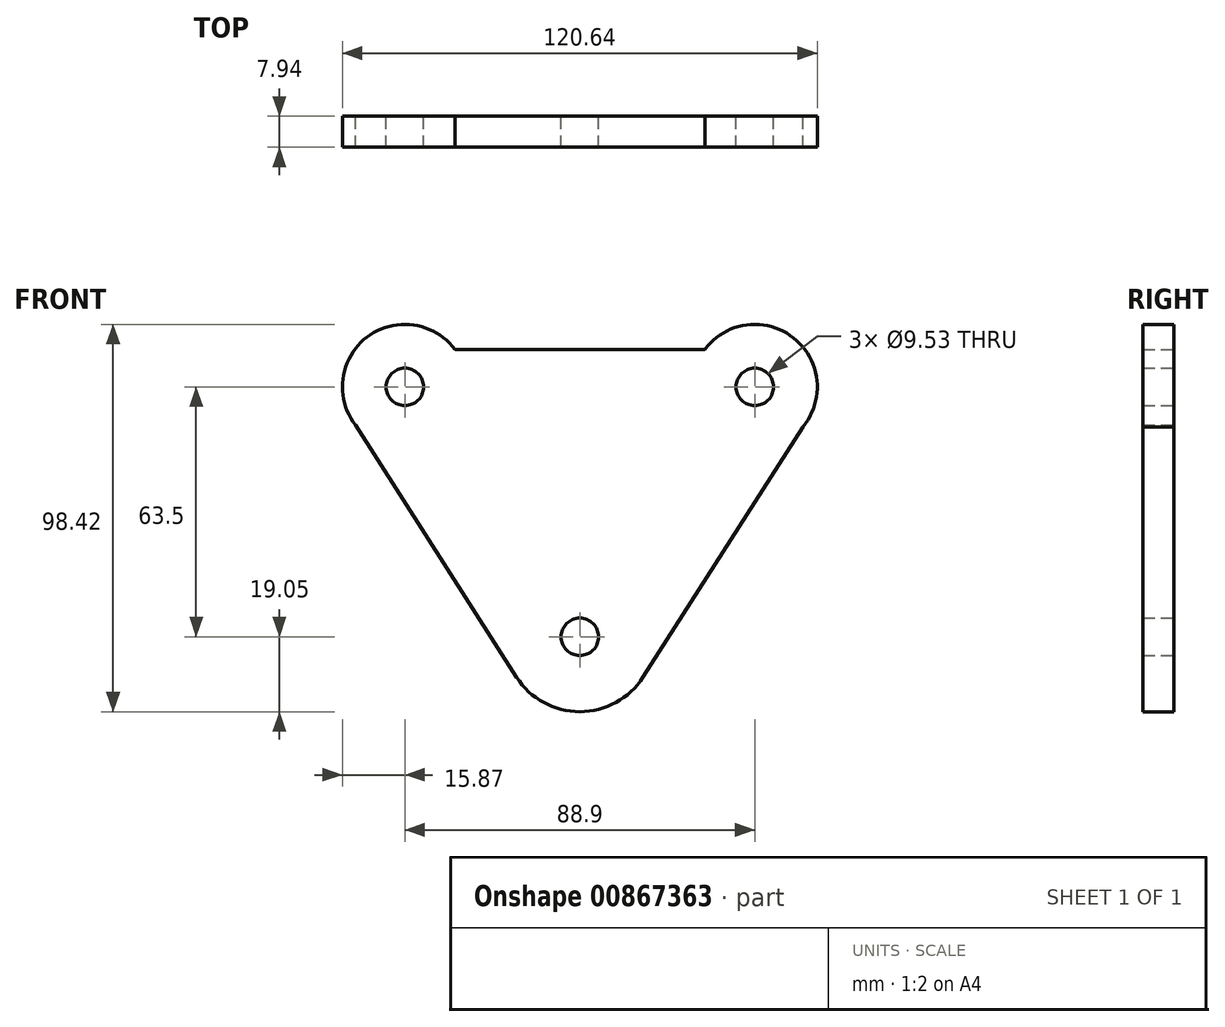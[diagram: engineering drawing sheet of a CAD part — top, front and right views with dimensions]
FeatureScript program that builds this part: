
annotation { "Feature Type Name" : "Feature", "Feature Type Description" : "" }
export const myFeature = defineFeature(function(context is Context, id is Id, definition is map)
    precondition{}
    {
        {
            var Q0;
            Q0=qCreatedBy(makeId("Front.planeOp"),FACE);
            var sketch = newSketch(context, id + "F0", { "sketchPlane" : qUnion([Q0])});
            skLineSegment(sketch, "E0", {"start": v(0, 0) * mm, "end": v(-88.9, 0) * mm});
            skLineSegment(sketch, "E1", {"start": v(-88.9, 0) * mm, "end": v(-88.9, 31.75) * mm});
            skLineSegment(sketch, "E2", {"start": v(-88.9, 0) * mm, "end": v(-88.9, -31.75) * mm});
            skCircle(sketch, "E3", {"center": v(-88.9, 31.75) * mm, "radius": 4.76 * mm});
            skLineSegment(sketch, "E4", {"start": v(-88.9, -31.75) * mm, "end": v(-44.45, -31.75) * mm});
            skCircle(sketch, "E5", {"center": v(-44.45, -31.75) * mm, "radius": 4.76 * mm});
            skLineSegment(sketch, "E6", {"start": v(0, 0) * mm, "end": v(-1.58, 0) * mm});
            skLineSegment(sketch, "E7", {"start": v(0, 0) * mm, "end": v(0, 31.75) * mm});
            skCircle(sketch, "E8", {"center": v(0, 31.75) * mm, "radius": 4.76 * mm});
            skArc(sketch, "E9", {"start": v(-76.2, 41.28) * mm, "mid": v(-98.53, 44.37) * mm, "end": v(-101.43, 22) * mm});
            skArc(sketch, "E10", {"start": v(12.21, 21.6) * mm, "mid": v(9.84, 44.2) * mm, "end": v(-12.7, 41.27) * mm});
            skArc(sketch, "E11", {"start": v(-60.5, -42.01) * mm, "mid": v(-44.44, -50.8) * mm, "end": v(-28.4, -42) * mm});
            skLineSegment(sketch, "E12", {"start": v(0, 31.75) * mm, "end": v(0, 41.27) * mm});
            skLineSegment(sketch, "E13", {"start": v(-12.7, 41.27) * mm, "end": v(-76.2, 41.27) * mm});
            skLineSegment(sketch, "E14", {"start": v(-103, 24.46) * mm, "end": v(-60.5, -42.01) * mm});
            skLineSegment(sketch, "E15", {"start": v(14.34, 24.94) * mm, "end": v(-28.4, -42) * mm});
            skSolve(sketch);
        }
        {
            var Q0;
            {var subQ0=sQuery(id+"F0.wireOp",EDGE,"E14");var subQ1=sQuery(id+"F0.wireOp",EDGE,"E9");var subQ2=makeQuery(id+"F0.imprint","INTERSECT",VERTEX,{"disambiguationData":[OD(0.0)],"derivedFrom":[subQ1,subQ0]});Q0=makeQuery(id+"F0.imprint","IMPRINT",FACE,{"disambiguationData":[TD([[makeQuery(id+"F0.imprint","IMPRINT",EDGE,{"disambiguationData":[TD([[subQ2,1.0]])],"derivedFrom":subQ1}),1.0]])]});}
            var Q1;
            {var subQ0=sQuery(id+"F0.wireOp",EDGE,"E15");var subQ1=sQuery(id+"F0.wireOp",EDGE,"E10");var subQ2=makeQuery(id+"F0.imprint","INTERSECT",VERTEX,{"disambiguationData":[OD(0.0)],"derivedFrom":[subQ1,subQ0]});Q1=makeQuery(id+"F0.imprint","IMPRINT",FACE,{"disambiguationData":[TD([[makeQuery(id+"F0.imprint","IMPRINT",EDGE,{"disambiguationData":[TD([[subQ2,-1.0]])],"derivedFrom":subQ1}),1.0]])]});}
            var Q2;
            Q2=makeQuery(id+"F0.imprint","IMPRINT",FACE,{"disambiguationData":[TD([[makeQuery(id+"F0.imprint","IMPRINT",EDGE,{"derivedFrom":sQuery(id+"F0.wireOp",EDGE,"E5")}),-1.0]])]});
            var Q3;
            Q3=makeQuery(id+"F0.imprint","IMPRINT",FACE,{"disambiguationData":[TD([[makeQuery(id+"F0.imprint","IMPRINT",EDGE,{"derivedFrom":sQuery(id+"F0.wireOp",EDGE,"E3")}),-1.0]])]});
            extrude(context, id + "F1", {"entities" : qUnion([Q0, Q1, Q2, Q3]), "depth" : 7.94 * mm, "offsetDistance" : 25.4 * mm});
        }
    });
